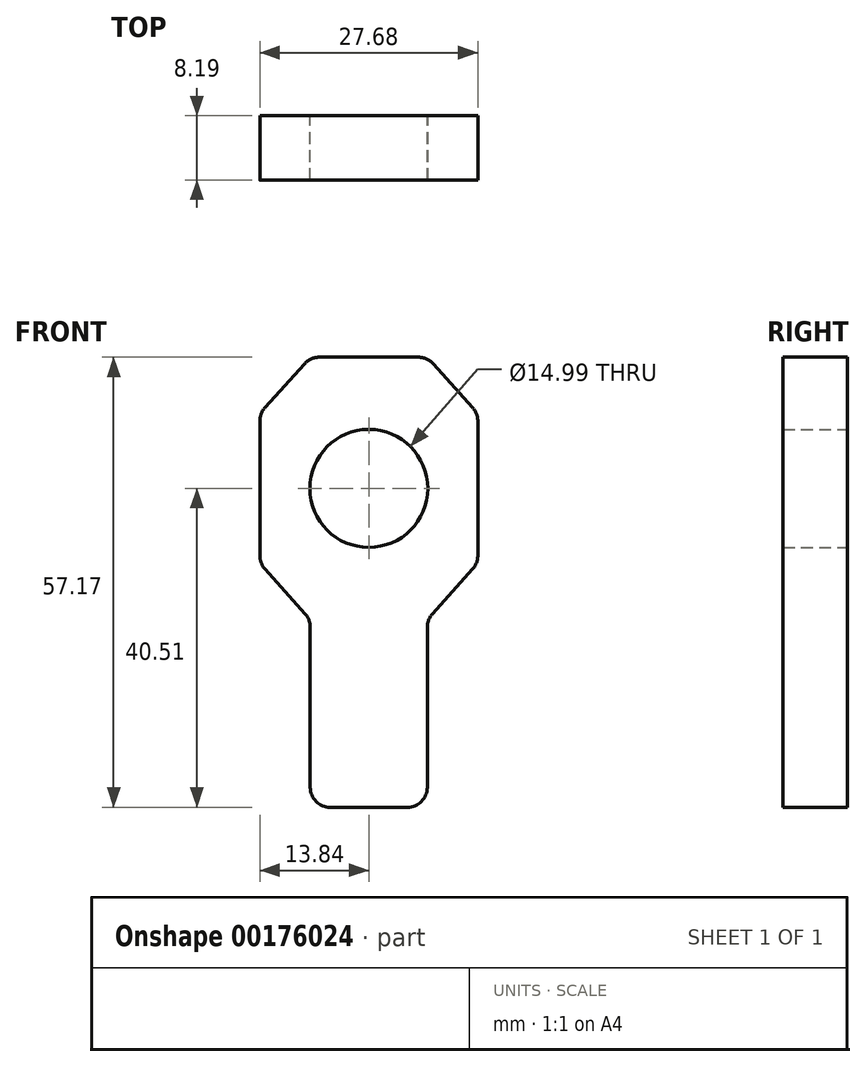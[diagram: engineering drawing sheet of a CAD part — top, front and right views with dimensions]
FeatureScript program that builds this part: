
annotation { "Feature Type Name" : "Feature", "Feature Type Description" : "" }
export const myFeature = defineFeature(function(context is Context, id is Id, definition is map)
    precondition{}
    {
        {
            var Q0;
            Q0=qCreatedBy(makeId("Front.planeOp"),FACE);
            var sketch = newSketch(context, id + "F0", { "sketchPlane" : qUnion([Q0])});
            skCircle(sketch, "E0", {"center": v(0, 0) * mm, "radius": 7.5 * mm});
            skLineSegment(sketch, "E1.bottom", {"start": v(-6.3, 16.66) * mm, "end": v(6.3, 16.66) * mm});
            skLineSegment(sketch, "E1.left", {"start": v(-13.84, 8.55) * mm, "end": v(-13.84, -8.55) * mm});
            skLineSegment(sketch, "E1.right", {"start": v(13.84, 8.55) * mm, "end": v(13.84, -8.55) * mm});
            skLineSegment(sketch, "E2", {"start": v(-8.2, 15.82) * mm, "end": v(-13.2, 10.25) * mm});
            skPoint(sketch, "E3.orphan", {"position": v(-13.84, 16.66) * mm});
            skLineSegment(sketch, "E4.MirrorCS", {"start": v(8.2, 15.82) * mm, "end": v(13.2, 10.25) * mm});
            skPoint(sketch, "E5.orphan", {"position": v(13.84, 16.66) * mm});
            skLineSegment(sketch, "E6", {"start": v(-4.9, -40.51) * mm, "end": v(4.9, -40.51) * mm});
            skLineSegment(sketch, "E7.MirrorCS", {"start": v(-8.08, -15.94) * mm, "end": v(-13.2, -10.25) * mm});
            skLineSegment(sketch, "E8.MirrorCS", {"start": v(8.08, -15.94) * mm, "end": v(13.2, -10.25) * mm});
            skLineSegment(sketch, "E9", {"start": v(-7.43, -17.64) * mm, "end": v(-7.43, -37.97) * mm});
            skLineSegment(sketch, "E10", {"start": v(7.43, -17.64) * mm, "end": v(7.43, -37.97) * mm});
            skPoint(sketch, "E11.visualSharp", {"position": v(-7.43, 16.66) * mm});
            skArc(sketch, "E11.filletArc", {"start": v(-6.3, 16.66) * mm, "mid": v(-7.34, 16.44) * mm, "end": v(-8.2, 15.82) * mm});
            skPoint(sketch, "E12.visualSharp", {"position": v(7.43, 16.66) * mm});
            skArc(sketch, "E12.filletArc", {"start": v(8.2, 15.82) * mm, "mid": v(7.34, 16.44) * mm, "end": v(6.3, 16.66) * mm});
            skPoint(sketch, "E13.visualSharp", {"position": v(13.84, 9.52) * mm});
            skArc(sketch, "E13.filletArc", {"start": v(13.84, 8.55) * mm, "mid": v(13.68, 9.46) * mm, "end": v(13.2, 10.25) * mm});
            skPoint(sketch, "E14.visualSharp", {"position": v(13.84, -9.52) * mm});
            skArc(sketch, "E14.filletArc", {"start": v(13.2, -10.25) * mm, "mid": v(13.68, -9.46) * mm, "end": v(13.84, -8.55) * mm});
            skPoint(sketch, "E15.visualSharp", {"position": v(7.43, -16.66) * mm});
            skArc(sketch, "E15.filletArc", {"start": v(8.08, -15.94) * mm, "mid": v(7.6, -16.73) * mm, "end": v(7.43, -17.64) * mm});
            skPoint(sketch, "E16.visualSharp", {"position": v(-7.43, -16.66) * mm});
            skArc(sketch, "E16.filletArc", {"start": v(-7.43, -17.64) * mm, "mid": v(-7.6, -16.73) * mm, "end": v(-8.08, -15.94) * mm});
            skPoint(sketch, "E17.visualSharp", {"position": v(-13.84, -9.52) * mm});
            skArc(sketch, "E17.filletArc", {"start": v(-13.84, -8.55) * mm, "mid": v(-13.68, -9.46) * mm, "end": v(-13.2, -10.25) * mm});
            skPoint(sketch, "E18.visualSharp", {"position": v(-13.84, 9.52) * mm});
            skArc(sketch, "E18.filletArc", {"start": v(-13.2, 10.25) * mm, "mid": v(-13.68, 9.46) * mm, "end": v(-13.84, 8.55) * mm});
            skPoint(sketch, "E19.visualSharp", {"position": v(-7.43, -40.51) * mm});
            skArc(sketch, "E19.filletArc", {"start": v(-7.43, -37.97) * mm, "mid": v(-6.7, -39.77) * mm, "end": v(-4.9, -40.51) * mm});
            skPoint(sketch, "E20.visualSharp", {"position": v(7.43, -40.51) * mm});
            skArc(sketch, "E20.filletArc", {"start": v(4.9, -40.51) * mm, "mid": v(6.7, -39.77) * mm, "end": v(7.43, -37.97) * mm});
            skSolve(sketch);
        }
        {
            var Q0;
            Q0=makeQuery(id+"F0.imprint","IMPRINT",FACE,{"disambiguationData":[TD([[makeQuery(id+"F0.imprint","IMPRINT",EDGE,{"derivedFrom":sQuery(id+"F0.wireOp",EDGE,"E0")}),-1.0]])]});
            extrude(context, id + "F1", {"entities" : qUnion([Q0]), "depth" : 8.2 * mm});
        }
    });
